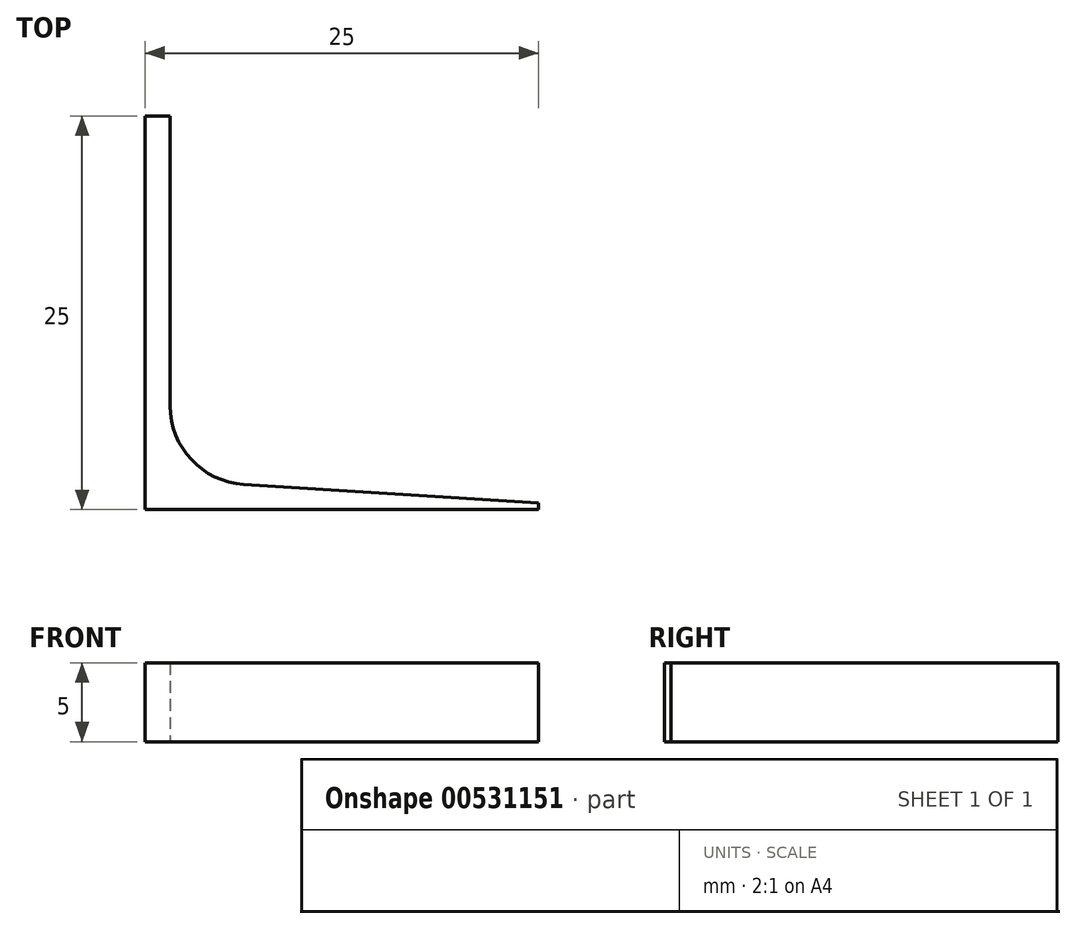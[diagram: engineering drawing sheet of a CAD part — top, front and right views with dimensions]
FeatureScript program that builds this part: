
annotation { "Feature Type Name" : "Feature", "Feature Type Description" : "" }
export const myFeature = defineFeature(function(context is Context, id is Id, definition is map)
    precondition{}
    {
        {
            var Q0;
            Q0=qCreatedBy(makeId("Top.planeOp"),FACE);
            var sketch = newSketch(context, id + "F0", { "sketchPlane" : qUnion([Q0])});
            skLineSegment(sketch, "E0", {"start": v(-8.36, 11.98) * mm, "end": v(-8.36, -13.02) * mm});
            skLineSegment(sketch, "E1", {"start": v(-8.36, -13.02) * mm, "end": v(16.64, -13.02) * mm});
            skLineSegment(sketch, "E2", {"start": v(16.64, -13.02) * mm, "end": v(16.64, -12.62) * mm});
            skLineSegment(sketch, "E3", {"start": v(16.64, -12.62) * mm, "end": v(-2.08, -11.42) * mm});
            skLineSegment(sketch, "E4", {"start": v(-6.76, -6.43) * mm, "end": v(-6.76, 11.98) * mm});
            skLineSegment(sketch, "E5", {"start": v(-6.76, 11.98) * mm, "end": v(-8.36, 11.98) * mm});
            skPoint(sketch, "E6.visualSharp", {"position": v(-6.76, -11.12) * mm});
            skArc(sketch, "E6.filletArc", {"start": v(-6.76, -6.43) * mm, "mid": v(-5.41, -9.85) * mm, "end": v(-2.08, -11.42) * mm});
            skLineSegment(sketch, "E7", {"start": v(-2.08, -11.42) * mm, "end": v(-2.08, -13.02) * mm, "construction": true});
            skSolve(sketch);
        }
        {
            var Q0;
            Q0=makeQuery(id+"F0.imprint","IMPRINT",FACE,{"disambiguationData":[TD([[makeQuery(id+"F0.imprint","IMPRINT",EDGE,{"derivedFrom":sQuery(id+"F0.wireOp",EDGE,"E0")}),1.0]])]});
            extrude(context, id + "F1", {"entities" : qUnion([Q0]), "depth" : 5 * mm, "offsetDistance" : 25 * mm});
        }
    });
